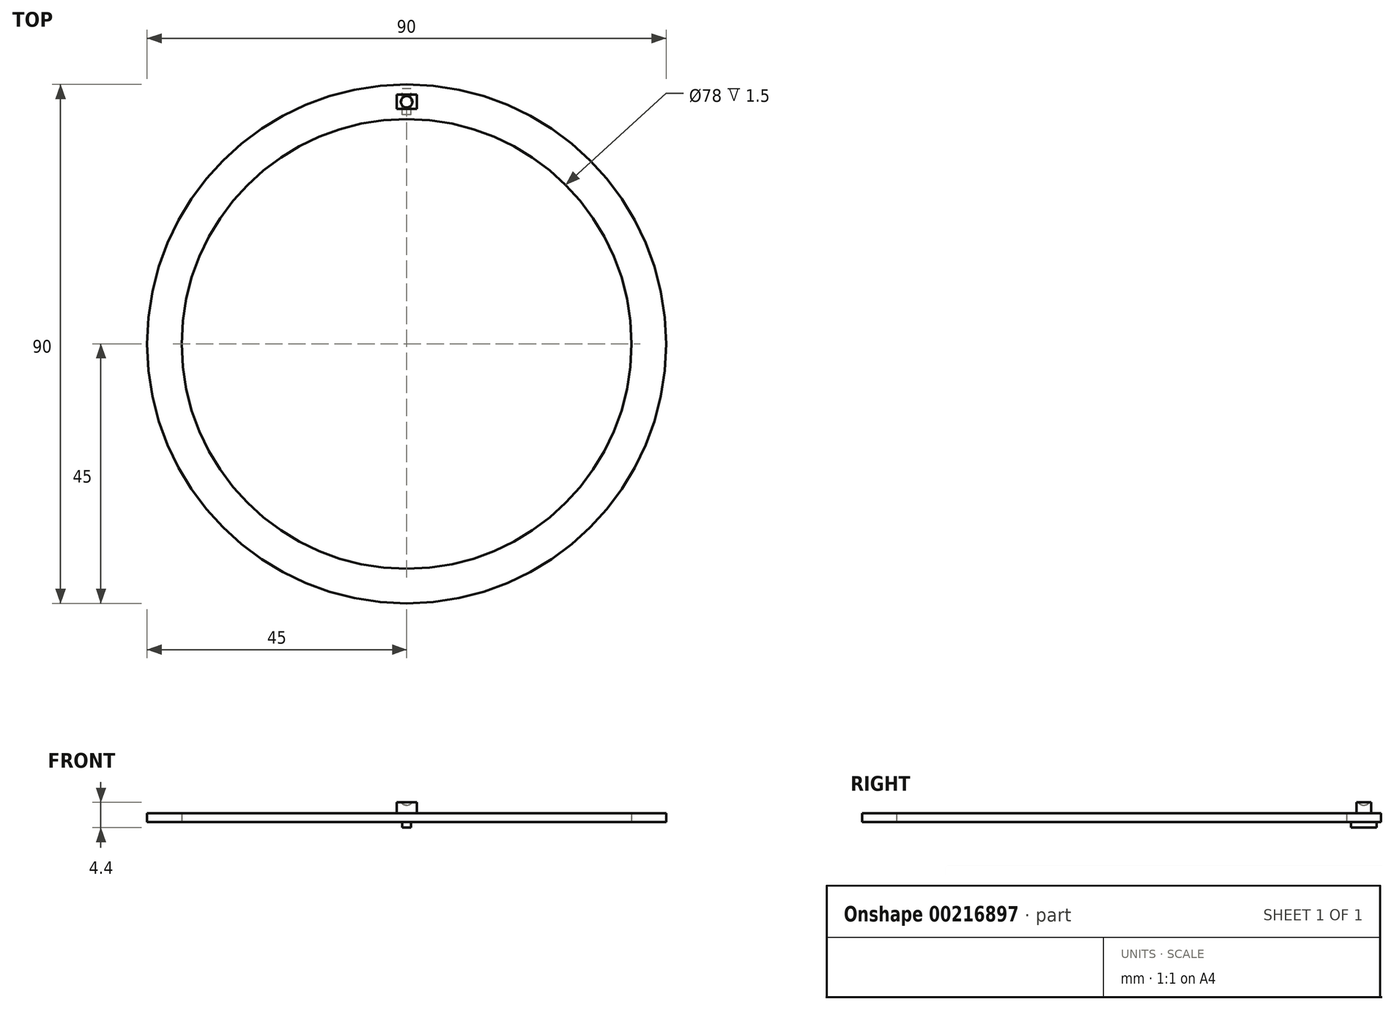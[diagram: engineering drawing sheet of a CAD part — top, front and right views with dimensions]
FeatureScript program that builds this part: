
annotation { "Feature Type Name" : "Feature", "Feature Type Description" : "" }
export const myFeature = defineFeature(function(context is Context, id is Id, definition is map)
    precondition{}
    {
        {
            var Q0;
            Q0=qCreatedBy(makeId("Top.planeOp"),FACE);
            var sketch = newSketch(context, id + "F0", { "sketchPlane" : qUnion([Q0])});
            skCircle(sketch, "E0", {"center": v(0, 0) * mm, "radius": 39 * mm});
            skCircle(sketch, "E1", {"center": v(0, 0) * mm, "radius": 45 * mm});
            skSolve(sketch);
        }
        {
            var Q0;
            Q0=makeQuery(id+"F0.imprint","IMPRINT",FACE,{"disambiguationData":[TD([[makeQuery(id+"F0.imprint","IMPRINT",EDGE,{"derivedFrom":sQuery(id+"F0.wireOp",EDGE,"E0")}),-1.0]])]});
            extrude(context, id + "F1", {"entities" : qUnion([Q0]), "depth" : 1.5 * mm});
        }
        {
            var Q0;
            Q0=makeQuery(id+"F1.opExtrude","CAP_FACE",FACE,{"disambiguationData":[OSD([sQuery(id+"F0.wireOp",EDGE,"E0"),sQuery(id+"F0.wireOp",EDGE,"E1")])],"isStart":false});
            var sketch = newSketch(context, id + "F2", { "sketchPlane" : qUnion([Q0])});
            skLineSegment(sketch, "E2", {"start": v(0, 39) * mm, "end": v(0, 45) * mm, "construction": true});
            skLineSegment(sketch, "E3.bottom", {"start": v(1.75, 40.75) * mm, "end": v(-1.75, 40.75) * mm});
            skLineSegment(sketch, "E3.top", {"start": v(1.75, 43.25) * mm, "end": v(-1.75, 43.25) * mm});
            skLineSegment(sketch, "E3.left", {"start": v(1.75, 40.75) * mm, "end": v(1.75, 43.25) * mm});
            skLineSegment(sketch, "E3.right", {"start": v(-1.75, 40.75) * mm, "end": v(-1.75, 43.25) * mm});
            skPoint(sketch, "E3.middle", {"position": v(0, 42) * mm});
            skSolve(sketch);
        }
        {
            var Q0;
            Q0=makeQuery(id+"F2.imprint","IMPRINT",FACE,{"disambiguationData":[TD([[makeQuery(id+"F2.imprint","IMPRINT",EDGE,{"derivedFrom":sQuery(id+"F2.wireOp",EDGE,"E3.bottom")}),-1.0]])]});
            extrude(context, id + "F3", {"entities" : qUnion([Q0]), "depth" : (3.4 - 1.5) * mm});
        }
        {
            var Q0;
            Q0=makeQuery(id+"F3.opExtrude","CAP_EDGE",EDGE,{"disambiguationData":[OSD([sQuery(id+"F2.wireOp",EDGE,"E3.left")])],"isStart":false});
            cPoint(context, id + "F4", {"entities" : qUnion([Q0]), "parameter" : 0.5});
        }
        {
            var Q0;
            Q0=makeQuery(id+"F3.opExtrude","SWEPT_FACE",FACE,{"disambiguationData":[OSD([sQuery(id+"F2.wireOp",EDGE,"E3.bottom")])]});
            var Q1;
            Q1 = qCreatedBy(id + "F4" ,VERTEX);
            cPlane(context, id + "F5", {"entities" : qUnion([Q0, Q1]), "cplaneType" : CPlaneType.PLANE_POINT, "offset" : 25 * mm, "width" : 150 * mm, "height" : 150 * mm});
        }
        {
            var Q0;
            Q0=qCreatedBy(id+"F5.planeOp",FACE);
            var sketch = newSketch(context, id + "F6", { "sketchPlane" : qUnion([Q0])});
            skArc(sketch, "E4", {"start": v(-1, 3.4) * mm, "mid": v(-0.56, 3.03) * mm, "end": v(0, 2.9) * mm});
            skLineSegment(sketch, "E5", {"start": v(-1, 3.4) * mm, "end": v(0, 3.4) * mm});
            skLineSegment(sketch, "E6", {"start": v(0, 2.9) * mm, "end": v(0, 3.4) * mm});
            skSolve(sketch);
        }
        {
            var Q0;
            Q0 = qSketchRegion(id + "F6", true);
            var Q1;
            Q1=sQuery(id+"F6.wireOp",EDGE,"E6");
            revolve(context, id + "F7", {"operationType" : NewBodyOperationType.REMOVE, "entities" : qUnion([Q0]), "axis" : qUnion([Q1]), "revolveType" : RevolveType.FULL, "oppositeDirection" : true});
        }
        {
            var Q0;
            Q0=makeQuery(id+"F1.opExtrude","CAP_FACE",FACE,{"disambiguationData":[OSD([sQuery(id+"F0.wireOp",EDGE,"E0"),sQuery(id+"F0.wireOp",EDGE,"E1")])],"isStart":true});
            var sketch = newSketch(context, id + "F8", { "sketchPlane" : qUnion([Q0])});
            skLineSegment(sketch, "E7.bottom", {"start": v(0.75, -39.75) * mm, "end": v(-0.75, -39.75) * mm});
            skLineSegment(sketch, "E7.top", {"start": v(0.75, -44.25) * mm, "end": v(-0.75, -44.25) * mm});
            skLineSegment(sketch, "E7.left", {"start": v(0.75, -39.75) * mm, "end": v(0.75, -44.25) * mm});
            skLineSegment(sketch, "E7.right", {"start": v(-0.75, -39.75) * mm, "end": v(-0.75, -44.25) * mm});
            skPoint(sketch, "E7.middle", {"position": v(0, -42) * mm});
            skLineSegment(sketch, "E8", {"start": v(0, -39) * mm, "end": v(0, -42) * mm, "construction": true});
            skLineSegment(sketch, "E9", {"start": v(0, -42) * mm, "end": v(0, -45) * mm, "construction": true});
            skSolve(sketch);
        }
        {
            var Q0;
            Q0=makeQuery(id+"F8.imprint","IMPRINT",FACE,{"disambiguationData":[TD([[makeQuery(id+"F8.imprint","IMPRINT",EDGE,{"derivedFrom":sQuery(id+"F8.wireOp",EDGE,"E7.bottom")}),1.0]])]});
            extrude(context, id + "F9", {"entities" : qUnion([Q0]), "depth" : 1 * mm});
        }
        {
            var Q0;
            Q0=makeQuery(id+"F1.opExtrude","CAP_FACE",FACE,{"disambiguationData":[OSD([sQuery(id+"F0.wireOp",EDGE,"E0"),sQuery(id+"F0.wireOp",EDGE,"E1")])],"isStart":false});
            var sketch = newSketch(context, id + "F10", { "sketchPlane" : qUnion([Q0])});
            skLineSegment(sketch, "E10", {"start": v(0, -39) * mm, "end": v(0, -45) * mm, "construction": true});
            skPoint(sketch, "E11", {"position": v(0, -42) * mm});
            skLineSegment(sketch, "E12", {"start": v(0, 0) * mm, "end": v(-5.1, -38.67) * mm, "construction": true});
            skCircle(sketch, "E13.0", {"center": v(0, 0) * mm, "radius": 39 * mm, "construction": true});
            skLineSegment(sketch, "E14", {"start": v(-5.1, -38.67) * mm, "end": v(-5.87, -44.62) * mm, "construction": true});
            skPoint(sketch, "E15", {"position": v(-5.48, -41.64) * mm});
            skSolve(sketch);
        }
        {
            var Q0;
            Q0=makeQuery(id+"F1.opExtrude","CAP_FACE",FACE,{"disambiguationData":[OSD([sQuery(id+"F0.wireOp",EDGE,"E0"),sQuery(id+"F0.wireOp",EDGE,"E1")])],"isStart":true});
            var sketch = newSketch(context, id + "F11", { "sketchPlane" : qUnion([Q0])});
            skPoint(sketch, "E16.0", {"position": v(-5.48, 41.64) * mm});
            skSolve(sketch);
        }
    });
